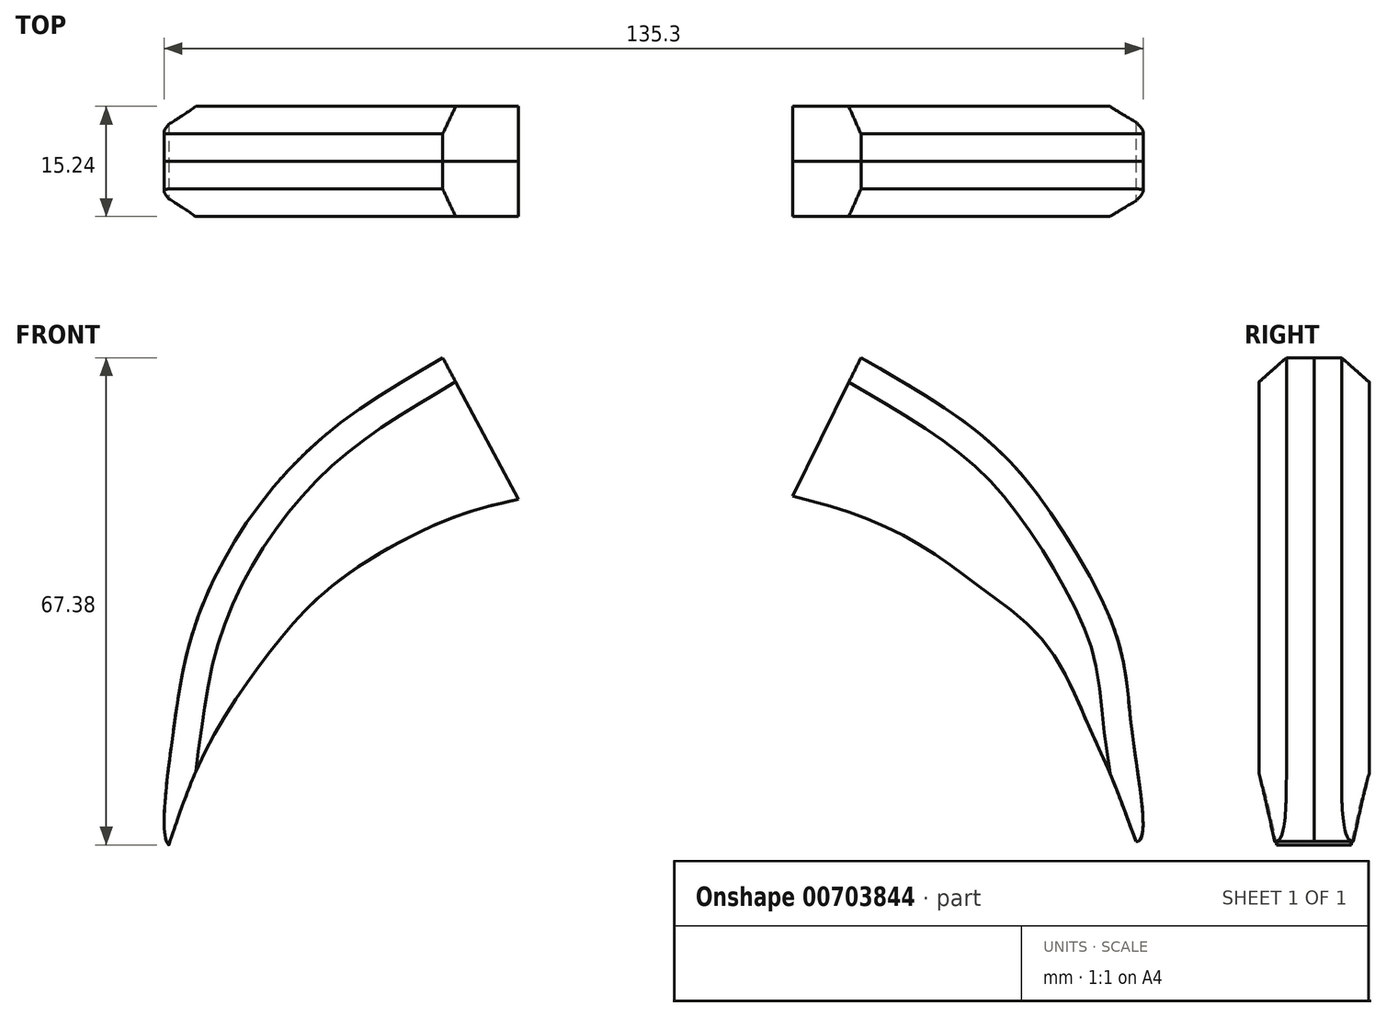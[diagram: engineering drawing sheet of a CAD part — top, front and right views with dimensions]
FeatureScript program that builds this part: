
annotation { "Feature Type Name" : "Feature", "Feature Type Description" : "" }
export const myFeature = defineFeature(function(context is Context, id is Id, definition is map)
    precondition{}
    {
        {
            var Q0;
            Q0=qCreatedBy(makeId("Front.planeOp"),FACE);
            var sketch = newSketch(context, id + "F0", { "sketchPlane" : qUnion([Q0])});
            skFitSpline(sketch, "E0", {"points": [v(28.63, 24.44) * mm, v(44.59, 14.28) * mm, v(54.56, 3.4) * mm, v(64, -14.2) * mm, v(66.17, -27.98) * mm, v(67.02, -42.39) * mm, v(58.4, -34.45) * mm, v(45.24, -23.86) * mm, v(30.95, -16.56) * mm, v(20.16, -13.67) * mm, v(10.58, -12.15) * mm], "startDerivative": vector(151.67, -87.38) * mm, "endDerivative": vector(-117, 17.02) * mm});
            skLineSegment(sketch, "E1", {"start": v(10.58, -12.15) * mm, "end": v(28.63, 24.44) * mm});
            skLineSegment(sketch, "E2", {"start": v(-29.18, 24.44) * mm, "end": v(-9.63, -12.15) * mm});
            skFitSpline(sketch, "E3", {"points": [v(-29.18, 24.44) * mm, v(-45.76, 13.42) * mm, v(-57.33, 0) * mm, v(-63.74, -13.63) * mm, v(-66.72, -29.43) * mm, v(-66.87, -43.03) * mm, v(-59.05, -35.22) * mm, v(-48.1, -25.68) * mm, v(-38.1, -19.58) * mm, v(-27.3, -15.04) * mm, v(-17.45, -12.7) * mm, v(-9.63, -12.15) * mm], "startDerivative": vector(-157.5, -92.28) * mm, "endDerivative": vector(109.56, 3.6) * mm});
            skSolve(sketch);
        }
        {
            var Q0;
            Q0=makeQuery(id+"F0.imprint","IMPRINT",FACE,{"disambiguationData":[TD([[makeQuery(id+"F0.imprint","IMPRINT",EDGE,{"derivedFrom":sQuery(id+"F0.wireOp",EDGE,"E2")}),-1.0]])]});
            var Q1;
            Q1=makeQuery(id+"F0.imprint","IMPRINT",FACE,{"disambiguationData":[TD([[makeQuery(id+"F0.imprint","IMPRINT",EDGE,{"derivedFrom":sQuery(id+"F0.wireOp",EDGE,"E0")}),-1.0]])]});
            extrude(context, id + "F1", {"entities" : qUnion([Q0, Q1]), "depth" : 7.62 * mm, "offsetDistance" : 25.4 * mm});
        }
        {
            var Q0;
            Q0=makeQuery(id+"F1.opExtrude","CAP_FACE",FACE,{"disambiguationData":[OSD([sQuery(id+"F0.wireOp",EDGE,"E2"),sQuery(id+"F0.wireOp",EDGE,"E3")])],"isStart":true});
            var Q1;
            Q1=makeQuery(id+"F1.opExtrude","CAP_FACE",FACE,{"disambiguationData":[OSD([sQuery(id+"F0.wireOp",EDGE,"E0"),sQuery(id+"F0.wireOp",EDGE,"E1")])],"isStart":true});
            extrude(context, id + "F2", {"entities" : qUnion([Q0, Q1]), "depth" : 7.62 * mm, "offsetDistance" : 25.4 * mm});
        }
        {
            var Q0;
            Q0=makeQuery(id+"F1.opExtrude","CAP_FACE",FACE,{"disambiguationData":[OSD([sQuery(id+"F0.wireOp",EDGE,"E2"),sQuery(id+"F0.wireOp",EDGE,"E3")])],"isStart":false});
            var sketch = newSketch(context, id + "F3", { "sketchPlane" : qUnion([Q0])});
            skFitSpline(sketch, "E4", {"points": [v(-18.71, 4.84) * mm, v(-27.4, 2.47) * mm, v(-39.68, -3.73) * mm, v(-48.13, -10.46) * mm, v(-54.97, -18.8) * mm, v(-62.09, -30.17) * mm, v(-67.02, -42.94) * mm], "startDerivative": vector(-56.78, -12.31) * mm, "endDerivative": vector(-24.22, -72.49) * mm});
            skSolve(sketch);
        }
        {
            var Q0;
            Q0=makeQuery(id+"F1.opExtrude","CAP_FACE",FACE,{"disambiguationData":[OSD([sQuery(id+"F0.wireOp",EDGE,"E0"),sQuery(id+"F0.wireOp",EDGE,"E1")])],"isStart":false});
            var sketch = newSketch(context, id + "F4", { "sketchPlane" : qUnion([Q0])});
            skFitSpline(sketch, "E5", {"points": [v(19.18, 5.3) * mm, v(29.27, 2.24) * mm, v(38.36, -2.44) * mm, v(45.81, -7.8) * mm, v(54.38, -15.43) * mm, v(59.93, -26.08) * mm, v(62.96, -32.83) * mm, v(66.63, -42.47) * mm], "startDerivative": vector(70, -18.2) * mm, "endDerivative": vector(26.01, -71.26) * mm});
            skSolve(sketch);
        }
        {
            var Q0;
            {var subQ0=sQuery(id+"F3.wireOp",EDGE,"E4");Q0=makeQuery(id+"F3.imprint","IMPRINT",FACE,{"disambiguationData":[TD([[makeQuery(id+"F3.imprint","IMPRINT",EDGE,{"derivedFrom":subQ0}),1.0]])]});}
            extrude(context, id + "F5", {"entities" : qUnion([Q0]), "operationType" : NewBodyOperationType.REMOVE, "oppositeDirection" : true, "depth" : 25.4 * mm, "offsetDistance" : 25.4 * mm});
        }
        {
            var Q0;
            {var subQ0=sQuery(id+"F4.wireOp",EDGE,"E5");Q0=makeQuery(id+"F4.imprint","IMPRINT",FACE,{"disambiguationData":[TD([[makeQuery(id+"F4.imprint","IMPRINT",EDGE,{"derivedFrom":subQ0}),-1.0]])]});}
            extrude(context, id + "F6", {"entities" : qUnion([Q0]), "operationType" : NewBodyOperationType.REMOVE, "oppositeDirection" : true, "depth" : 25.4 * mm, "offsetDistance" : 25.4 * mm});
        }
        {
            var Q0;
            Q0=makeQuery(id+"F1.opExtrude","CAP_EDGE",EDGE,{"disambiguationData":[OSD([sQuery(id+"F0.wireOp",EDGE,"E3")])],"isStart":false});
            var Q1;
            Q1=makeQuery(id+"F2.opExtrude","CAP_EDGE",EDGE,{"disambiguationData":[OSD([sQuery(id+"F0.wireOp",EDGE,"E3")])],"isStart":false});
            var Q2;
            Q2=makeQuery(id+"F1.opExtrude","CAP_EDGE",EDGE,{"disambiguationData":[OSD([sQuery(id+"F0.wireOp",EDGE,"E0")])],"isStart":false});
            var Q3;
            Q3=makeQuery(id+"F2.opExtrude","CAP_EDGE",EDGE,{"disambiguationData":[OSD([sQuery(id+"F0.wireOp",EDGE,"E0")])],"isStart":false});
            chamfer(context, id + "F7", {"entities" : qUnion([Q0, Q1, Q2, Q3]), "width" : 3.8 * mm, "tangentPropagation" : true});
        }
    });
